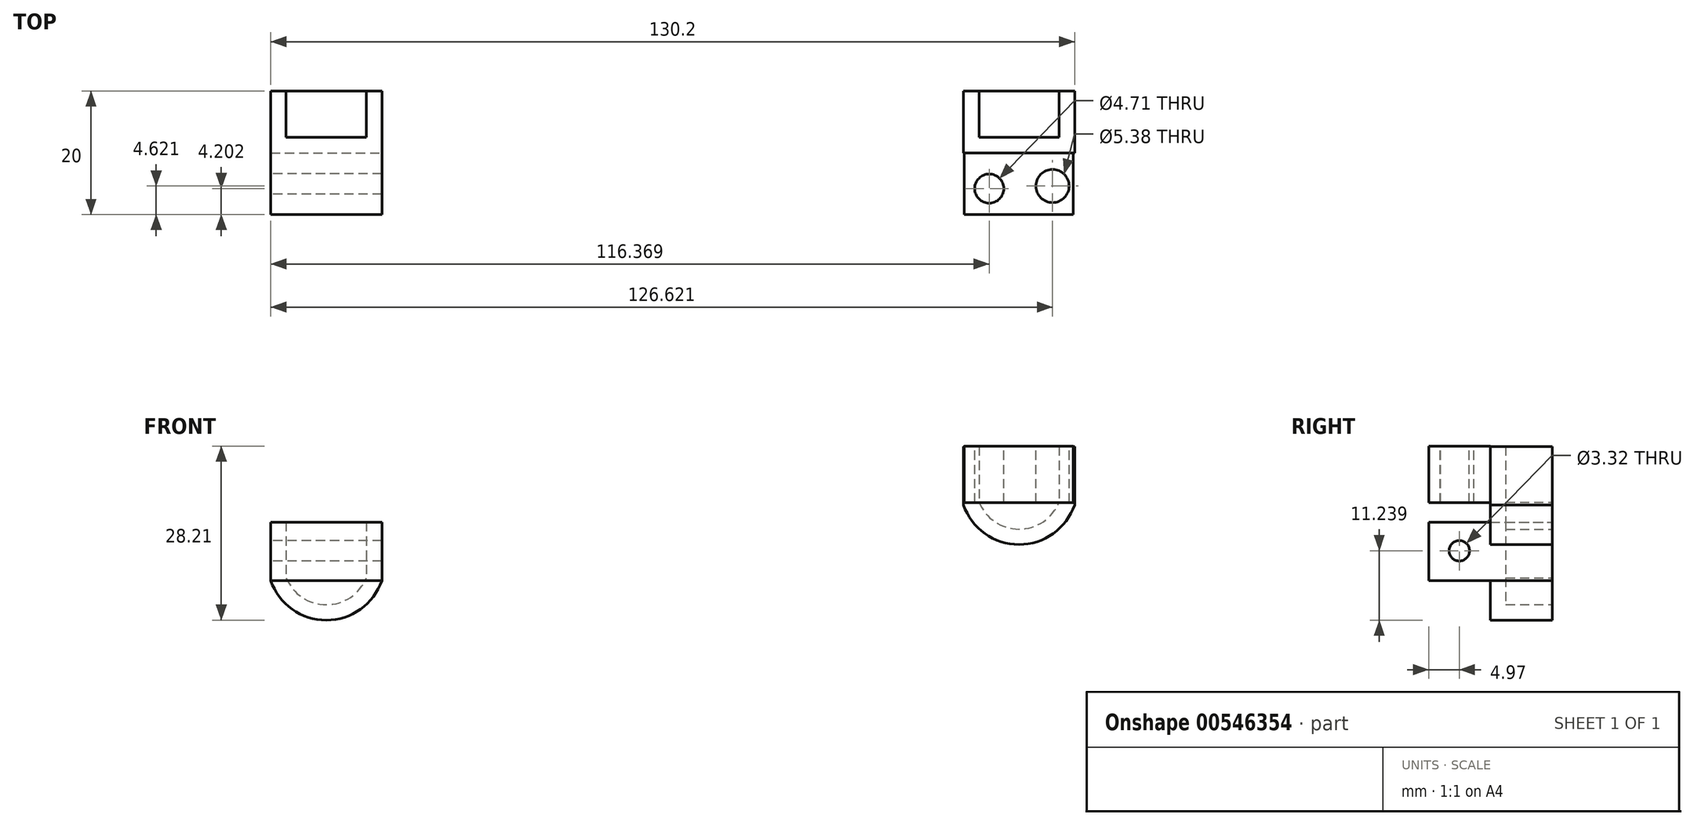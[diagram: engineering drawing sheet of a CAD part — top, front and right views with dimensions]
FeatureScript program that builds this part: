
annotation { "Feature Type Name" : "Feature", "Feature Type Description" : "" }
export const myFeature = defineFeature(function(context is Context, id is Id, definition is map)
    precondition{}
    {
        {
            var Q0;
            Q0=qCreatedBy(makeId("Front.planeOp"),FACE);
            var sketch = newSketch(context, id + "F0", { "sketchPlane" : qUnion([Q0])});
            skLineSegment(sketch, "E0.bottom", {"start": v(-70.31, 35.51) * mm, "end": v(-52.31, 35.51) * mm});
            skLineSegment(sketch, "E0.top", {"start": v(-70.31, 26.06) * mm, "end": v(-52.31, 26.06) * mm});
            skLineSegment(sketch, "E0.left", {"start": v(-70.31, 35.51) * mm, "end": v(-70.31, 26.06) * mm});
            skLineSegment(sketch, "E0.right", {"start": v(-52.31, 35.51) * mm, "end": v(-52.31, 26.06) * mm});
            skArc(sketch, "E1", {"start": v(-70.31, 26.06) * mm, "mid": v(-61.31, 19.64) * mm, "end": v(-52.31, 26.06) * mm});
            skLineSegment(sketch, "E2.bottom", {"start": v(41.89, 47.77) * mm, "end": v(59.89, 47.77) * mm});
            skLineSegment(sketch, "E2.top", {"start": v(41.89, 38.32) * mm, "end": v(59.89, 38.32) * mm});
            skLineSegment(sketch, "E2.left", {"start": v(41.89, 47.77) * mm, "end": v(41.89, 38.32) * mm});
            skLineSegment(sketch, "E2.right", {"start": v(59.89, 47.77) * mm, "end": v(59.89, 38.32) * mm});
            skArc(sketch, "E3", {"start": v(41.89, 38.32) * mm, "mid": v(50.89, 31.9) * mm, "end": v(59.89, 38.32) * mm});
            skSolve(sketch);
        }
        {
            var Q0;
            Q0=qSketchRegion(id+"F0",true);
            extrude(context, id + "F1", {"entities" : qUnion([Q0]), "depth" : 10 * mm, "offsetDistance" : 25 * mm});
        }
        {
            var Q0;
            Q0=makeQuery(id+"F1.opExtrude","SWEPT_FACE",FACE,{"disambiguationData":[OSD([sQuery(id+"F0.wireOp",EDGE,"E0.bottom")])]});
            var Q1;
            Q1=makeQuery(id+"F1.opExtrude","CAP_FACE",FACE,{"disambiguationData":[OSD([sQuery(id+"F0.wireOp",EDGE,"E0.bottom"),sQuery(id+"F0.wireOp",EDGE,"E0.left"),sQuery(id+"F0.wireOp",EDGE,"E0.right"),sQuery(id+"F0.wireOp",EDGE,"E1")])],"isStart":true});
            var Q2;
            Q2=makeQuery(id+"F1.opExtrude","CAP_FACE",FACE,{"disambiguationData":[OSD([sQuery(id+"F0.wireOp",EDGE,"E2.bottom"),sQuery(id+"F0.wireOp",EDGE,"E2.left"),sQuery(id+"F0.wireOp",EDGE,"E2.right"),sQuery(id+"F0.wireOp",EDGE,"E3")])],"isStart":true});
            var Q3;
            Q3=makeQuery(id+"F1.opExtrude","SWEPT_FACE",FACE,{"disambiguationData":[OSD([sQuery(id+"F0.wireOp",EDGE,"E2.bottom")])]});
            shell(context, id + "F2", {"entities" : qUnion([Q0, Q1, Q2, Q3]), "thickness" : 2.5 * mm});
        }
        {
            var Q0;
            Q0=makeQuery(id+"F1.opExtrude","CAP_FACE",FACE,{"disambiguationData":[OSD([sQuery(id+"F0.wireOp",EDGE,"E0.bottom"),sQuery(id+"F0.wireOp",EDGE,"E0.left"),sQuery(id+"F0.wireOp",EDGE,"E0.right"),sQuery(id+"F0.wireOp",EDGE,"E1")])],"isStart":false});
            var sketch = newSketch(context, id + "F3", { "sketchPlane" : qUnion([Q0])});
            skLineSegment(sketch, "E4.bottom", {"start": v(-70.31, 35.51) * mm, "end": v(-52.31, 35.51) * mm});
            skPoint(sketch, "E4.right.end.orphan", {"position": v(-52.31, 15.1) * mm});
            skPoint(sketch, "E4.left.end.orphan", {"position": v(-70.31, 15.1) * mm});
            skLineSegment(sketch, "E5.top", {"start": v(-70.31, 26.06) * mm, "end": v(-52.31, 26.06) * mm});
            skLineSegment(sketch, "E5.left", {"start": v(-70.31, 35.51) * mm, "end": v(-70.31, 26.06) * mm});
            skLineSegment(sketch, "E5.right", {"start": v(-52.31, 35.51) * mm, "end": v(-52.31, 26.06) * mm});
            skLineSegment(sketch, "E6.bottom", {"start": v(42.04, 38.7) * mm, "end": v(59.69, 38.7) * mm});
            skLineSegment(sketch, "E6.top", {"start": v(42.04, 47.85) * mm, "end": v(59.69, 47.85) * mm});
            skLineSegment(sketch, "E6.left", {"start": v(42.04, 38.7) * mm, "end": v(42.04, 47.85) * mm});
            skLineSegment(sketch, "E6.right", {"start": v(59.69, 38.7) * mm, "end": v(59.69, 47.85) * mm});
            skSolve(sketch);
        }
        {
            var Q0;
            Q0=qSketchRegion(id+"F3",true);
            extrude(context, id + "F4", {"entities" : qUnion([Q0]), "operationType" : NewBodyOperationType.ADD, "depth" : 10 * mm, "offsetDistance" : 25 * mm});
        }
        {
            var Q0;
            Q0=makeQuery(id+"F4.opExtrude","SWEPT_FACE",FACE,{"disambiguationData":[OSD([sQuery(id+"F3.wireOp",EDGE,"E6.top")])]});
            var sketch = newSketch(context, id + "F5", { "sketchPlane" : qUnion([Q0])});
            skCircle(sketch, "E7", {"center": v(56.31, -15.38) * mm, "radius": 2.69 * mm});
            skCircle(sketch, "E8", {"center": v(46.06, -15.8) * mm, "radius": 2.35 * mm});
            skSolve(sketch);
        }
        {
            var Q0;
            Q0=qSketchRegion(id+"F5",true);
            extrude(context, id + "F6", {"entities" : qUnion([Q0]), "operationType" : NewBodyOperationType.REMOVE, "oppositeDirection" : true, "depth" : 25 * mm, "offsetDistance" : 25 * mm});
        }
        {
            var Q0;
            Q0=makeQuery(id+"F4.opExtrude","SWEPT_FACE",FACE,{"disambiguationData":[OSD([sQuery(id+"F3.wireOp",EDGE,"E5.left")])]});
            var sketch = newSketch(context, id + "F7", { "sketchPlane" : qUnion([Q0])});
            skCircle(sketch, "E9", {"center": v(15.03, 30.88) * mm, "radius": 1.66 * mm});
            skSolve(sketch);
        }
        {
            var Q0;
            Q0=qSketchRegion(id+"F7",true);
            extrude(context, id + "F8", {"entities" : qUnion([Q0]), "operationType" : NewBodyOperationType.REMOVE, "oppositeDirection" : true, "depth" : 25 * mm, "offsetDistance" : 25 * mm});
        }
    });
